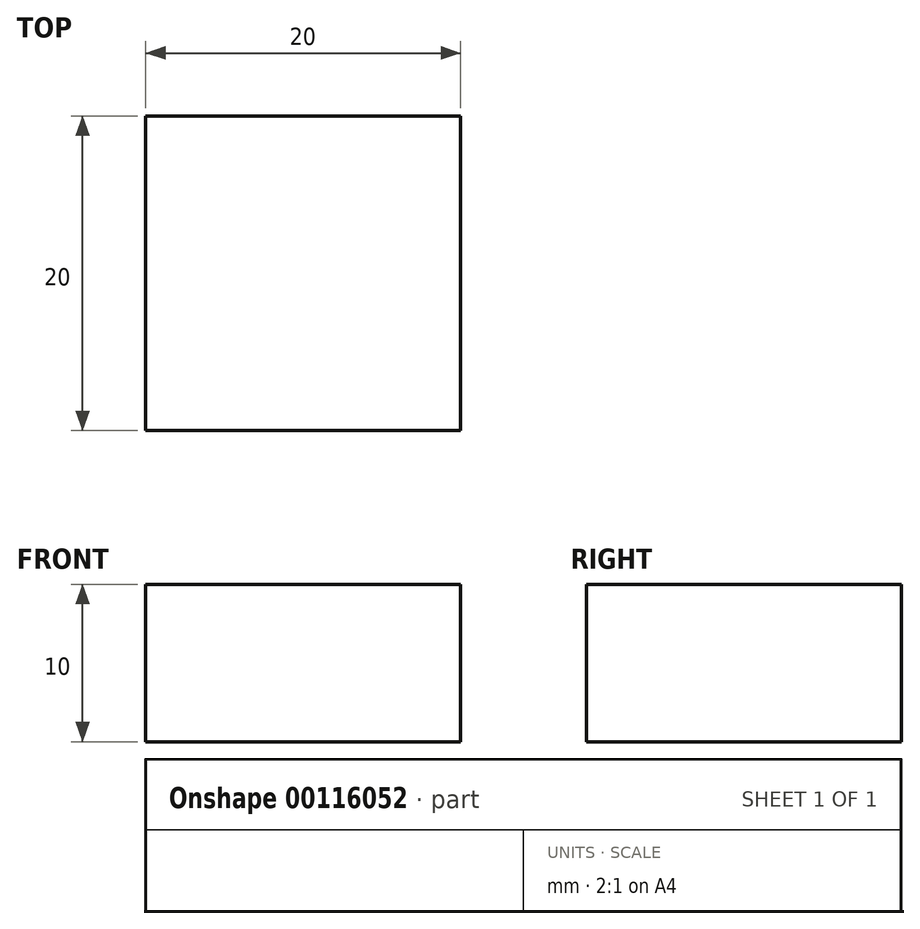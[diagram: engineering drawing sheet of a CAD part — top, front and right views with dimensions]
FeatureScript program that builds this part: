
annotation { "Feature Type Name" : "Feature", "Feature Type Description" : "" }
export const myFeature = defineFeature(function(context is Context, id is Id, definition is map)
    precondition{}
    {
        {
            var Q0;
            Q0=qCreatedBy(makeId("Top.planeOp"),FACE);
            var sketch = newSketch(context, id + "F0", { "sketchPlane" : qUnion([Q0])});
            skLineSegment(sketch, "E0.bottom", {"start": v(0, 0) * mm, "end": v(20, 0) * mm});
            skLineSegment(sketch, "E0.top", {"start": v(0, 20) * mm, "end": v(20, 20) * mm});
            skLineSegment(sketch, "E0.left", {"start": v(0, 0) * mm, "end": v(0, 20) * mm});
            skLineSegment(sketch, "E0.right", {"start": v(20, 0) * mm, "end": v(20, 20) * mm});
            skSolve(sketch);
        }
        {
            var Q0;
            Q0=makeQuery(id+"F0.imprint","IMPRINT",FACE,{"disambiguationData":[TD([[makeQuery(id+"F0.imprint","IMPRINT",EDGE,{"derivedFrom":sQuery(id+"F0.wireOp",EDGE,"E0.bottom")}),1.0]])]});
            extrude(context, id + "F1", {"entities" : qUnion([Q0]), "depth" : 10 * mm});
        }
    });
